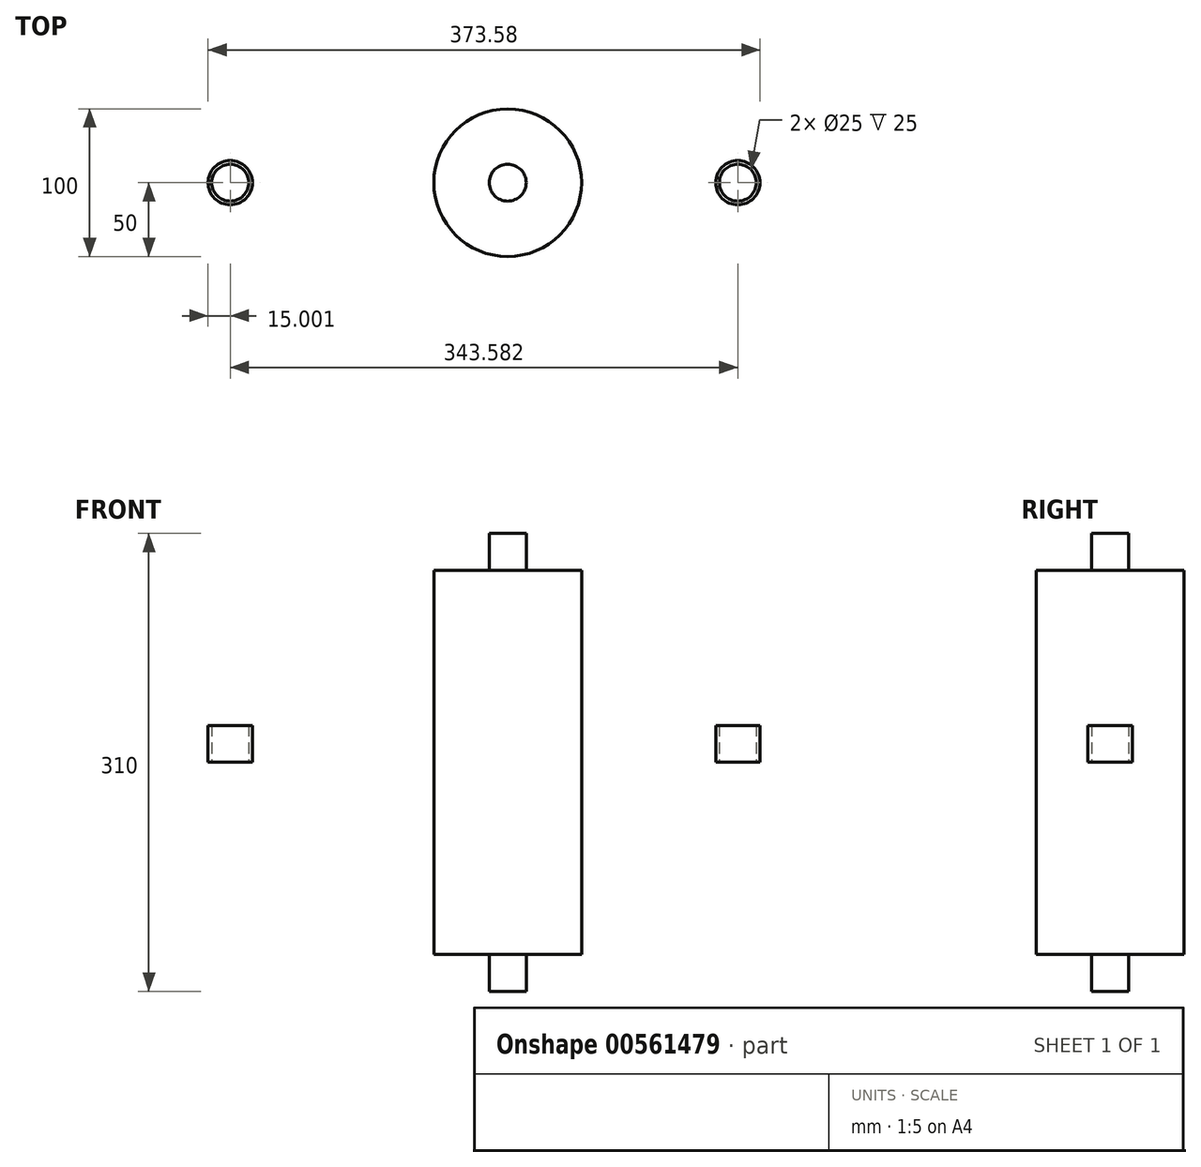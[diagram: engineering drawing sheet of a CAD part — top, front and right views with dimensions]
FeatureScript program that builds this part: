
annotation { "Feature Type Name" : "Feature", "Feature Type Description" : "" }
export const myFeature = defineFeature(function(context is Context, id is Id, definition is map)
    precondition{}
    {
        {
            var Q0;
            Q0=qCreatedBy(makeId("Top.planeOp"),FACE);
            var sketch = newSketch(context, id + "F0", { "sketchPlane" : qUnion([Q0])});
            skCircle(sketch, "E0", {"center": v(0, 0) * mm, "radius": 50 * mm});
            skCircle(sketch, "E1", {"center": v(0, 0) * mm, "radius": 12.5 * mm});
            skSolve(sketch);
        }
        {
            var Q0;
            Q0=makeQuery(id+"F0.imprint","IMPRINT",FACE,{"disambiguationData":[TD([[makeQuery(id+"F0.imprint","IMPRINT",EDGE,{"derivedFrom":sQuery(id+"F0.wireOp",EDGE,"E1")}),1.0]])]});
            extrude(context, id + "F1", {"entities" : qUnion([Q0]), "endBound" : BoundingType.SYMMETRIC, "depth" : 310 * mm, "offsetDistance" : 25 * mm});
        }
        {
            var Q0;
            Q0 = qSketchRegion(id + "F0", true);
            extrude(context, id + "F2", {"entities" : qUnion([Q0]), "operationType" : NewBodyOperationType.ADD, "endBound" : BoundingType.SYMMETRIC, "depth" : 260 * mm, "offsetDistance" : 25 * mm});
        }
        {
            var Q0;
            Q0=qCreatedBy(makeId("Top.planeOp"),FACE);
            var sketch = newSketch(context, id + "F3", { "sketchPlane" : qUnion([Q0])});
            skCircle(sketch, "E2", {"center": v(-187.8, 0) * mm, "radius": 15 * mm});
            skCircle(sketch, "E3", {"center": v(-187.8, 0) * mm, "radius": 12.5 * mm});
            skCircle(sketch, "E4", {"center": v(155.78, 0) * mm, "radius": 15 * mm});
            skCircle(sketch, "E5", {"center": v(155.78, 0) * mm, "radius": 12.5 * mm});
            skSolve(sketch);
        }
        {
            var Q0;
            Q0 = qSketchRegion(id + "F3", true);
            extrude(context, id + "F4", {"entities" : qUnion([Q0]), "depth" : 25 * mm, "offsetDistance" : 25 * mm});
        }
    });
